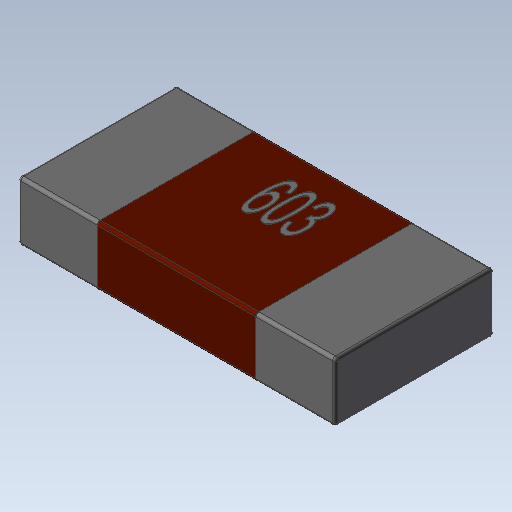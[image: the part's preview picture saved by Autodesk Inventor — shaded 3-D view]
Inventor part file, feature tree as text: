
AUTODESK INVENTOR PART (.ipt)
format: ipt  version: 2020 (Build 240168000, 168)  size: 249,856 bytes
history: native  units: in
note: dims shown in document units (in); Inventor stores cm internally (conversion verified against a paired STEP export)
features: extrude x1
ambient origin geometry x8: Origin, YZ Plane, XZ Plane, XY Plane, X Axis, Y Axis, Z Axis, Center Point
bodies: Solid1 (feature_tree)
feature tree (1):
  extrude  "Extrude2"  [1 undecoded]
note: 1 required parameter value undecoded (feature->parameter linkage not recoverable at this tier; creation-order binding heuristic only, values carry confidence <= 0.55)
